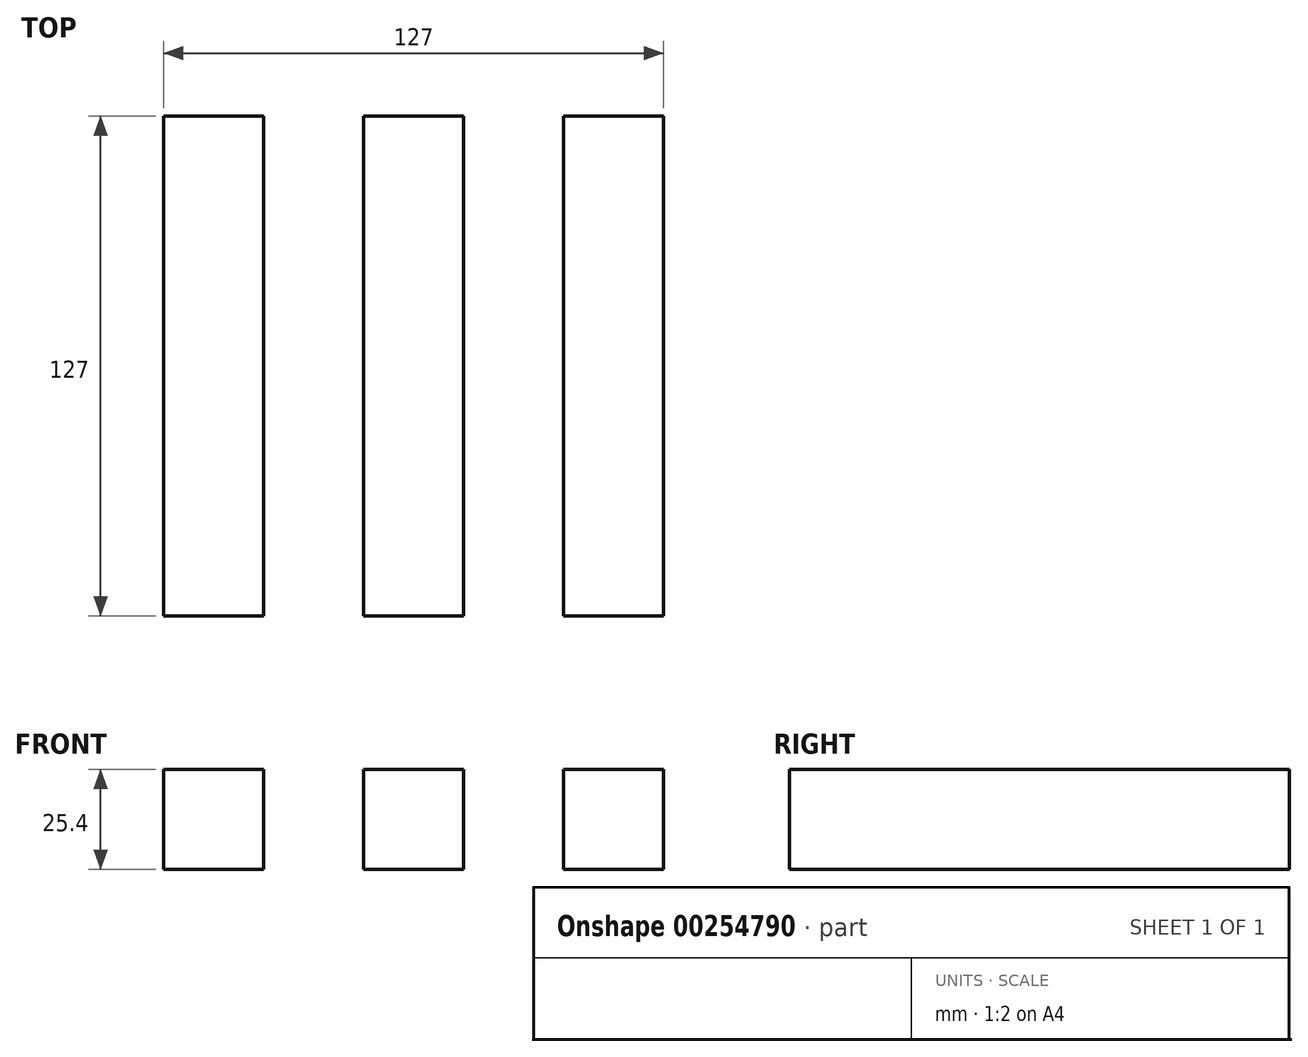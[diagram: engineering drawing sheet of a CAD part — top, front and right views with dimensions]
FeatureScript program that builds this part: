
annotation { "Feature Type Name" : "Feature", "Feature Type Description" : "" }
export const myFeature = defineFeature(function(context is Context, id is Id, definition is map)
    precondition{}
    {
        {
            var Q0;
            Q0=qCreatedBy(makeId("Front.planeOp"),FACE);
            var sketch = newSketch(context, id + "F0", { "sketchPlane" : qUnion([Q0])});
            skLineSegment(sketch, "E0", {"start": v(0, 0) * mm, "end": v(-50.8, 0) * mm});
            skLineSegment(sketch, "E1", {"start": v(0, 0) * mm, "end": v(50.8, 0) * mm});
            skLineSegment(sketch, "E2.bottom", {"start": v(-38.1, -12.7) * mm, "end": v(-63.5, -12.7) * mm});
            skLineSegment(sketch, "E2.top", {"start": v(-38.1, 12.7) * mm, "end": v(-63.5, 12.7) * mm});
            skLineSegment(sketch, "E2.left", {"start": v(-38.1, -12.7) * mm, "end": v(-38.1, 12.7) * mm});
            skLineSegment(sketch, "E2.right", {"start": v(-63.5, -12.7) * mm, "end": v(-63.5, 12.7) * mm});
            skPoint(sketch, "E2.middle", {"position": v(-50.8, 0) * mm});
            skLineSegment(sketch, "E3.bottom", {"start": v(-12.7, -12.7) * mm, "end": v(12.7, -12.7) * mm});
            skLineSegment(sketch, "E3.top", {"start": v(-12.7, 12.7) * mm, "end": v(12.7, 12.7) * mm});
            skLineSegment(sketch, "E3.left", {"start": v(-12.7, -12.7) * mm, "end": v(-12.7, 12.7) * mm});
            skLineSegment(sketch, "E3.right", {"start": v(12.7, -12.7) * mm, "end": v(12.7, 12.7) * mm});
            skPoint(sketch, "E3.middle", {"position": v(0, 0) * mm});
            skLineSegment(sketch, "E4.bottom", {"start": v(63.5, -12.7) * mm, "end": v(38.1, -12.7) * mm});
            skLineSegment(sketch, "E4.top", {"start": v(63.5, 12.7) * mm, "end": v(38.1, 12.7) * mm});
            skLineSegment(sketch, "E4.left", {"start": v(63.5, -12.7) * mm, "end": v(63.5, 12.7) * mm});
            skLineSegment(sketch, "E4.right", {"start": v(38.1, -12.7) * mm, "end": v(38.1, 12.7) * mm});
            skPoint(sketch, "E4.middle", {"position": v(50.8, 0) * mm});
            skSolve(sketch);
        }
        {
            var Q0;
            {var subQ3=sQuery(id+"F0.wireOp",EDGE,"E2.bottom");Q0=makeQuery(id+"F0.imprint","IMPRINT",FACE,{"disambiguationData":[TD([[makeQuery(id+"F0.imprint","IMPRINT",EDGE,{"derivedFrom":subQ3}),-1.0]])]});}
            var Q1;
            {var subQ1=sQuery(id+"F0.wireOp",EDGE,"E3.top");Q1=makeQuery(id+"F0.imprint","IMPRINT",FACE,{"disambiguationData":[TD([[makeQuery(id+"F0.imprint","IMPRINT",EDGE,{"derivedFrom":subQ1}),-1.0]])]});}
            var Q2;
            {var subQ1=sQuery(id+"F0.wireOp",EDGE,"E3.bottom");Q2=makeQuery(id+"F0.imprint","IMPRINT",FACE,{"disambiguationData":[TD([[makeQuery(id+"F0.imprint","IMPRINT",EDGE,{"derivedFrom":subQ1}),1.0]])]});}
            var Q3;
            {var subQ1=sQuery(id+"F0.wireOp",EDGE,"E4.bottom");Q3=makeQuery(id+"F0.imprint","IMPRINT",FACE,{"disambiguationData":[TD([[makeQuery(id+"F0.imprint","IMPRINT",EDGE,{"derivedFrom":subQ1}),-1.0]])]});}
            extrude(context, id + "F1", {"entities" : qUnion([Q0, Q1, Q2, Q3]), "endBound" : BoundingType.SYMMETRIC, "depth" : 127 * mm});
        }
    });
